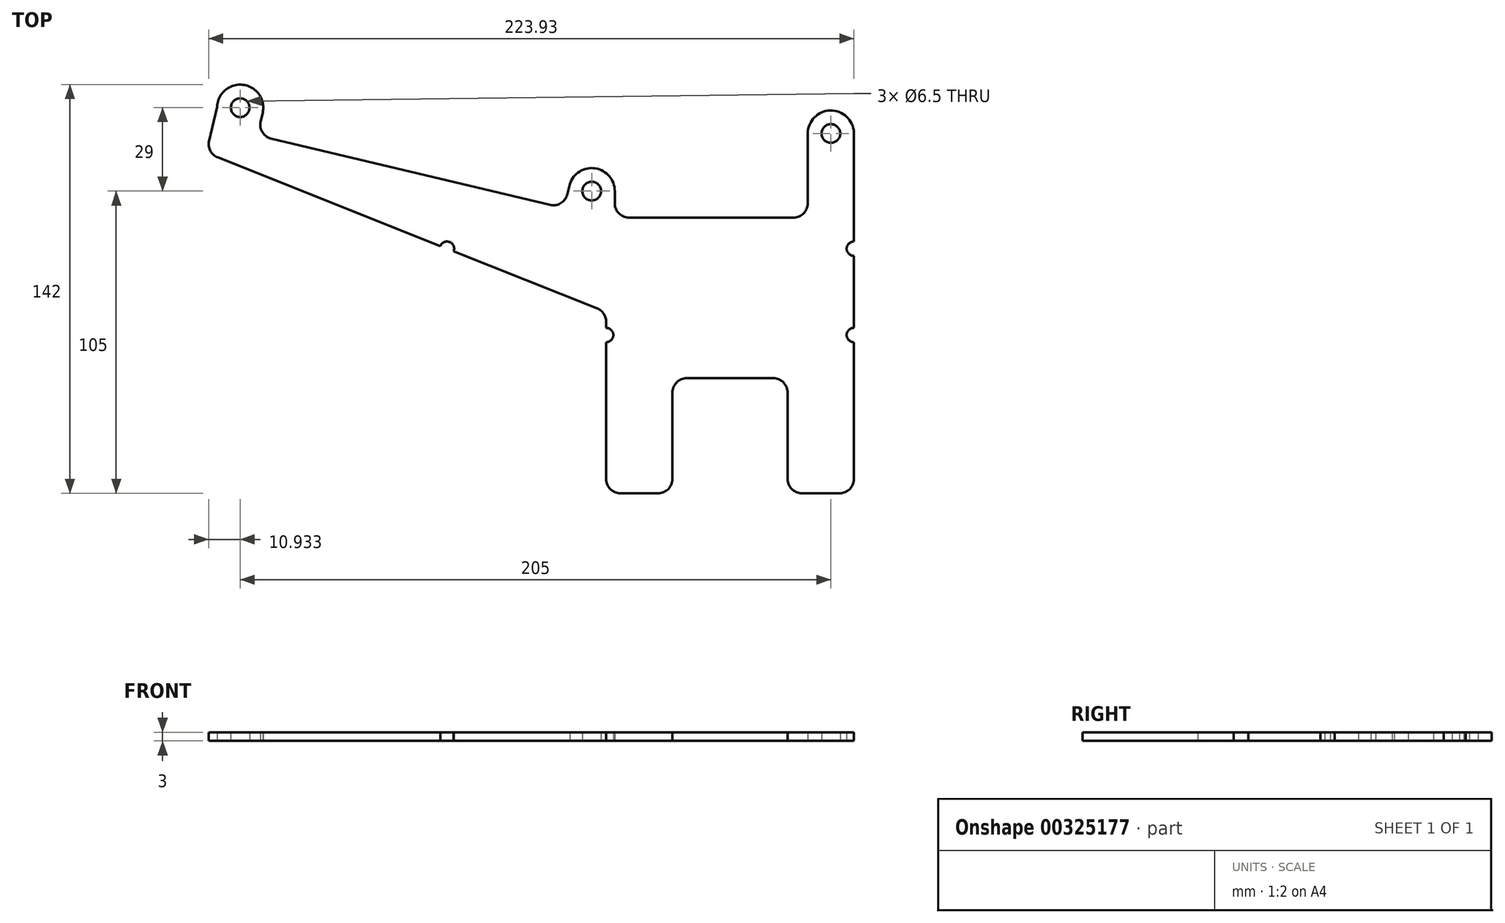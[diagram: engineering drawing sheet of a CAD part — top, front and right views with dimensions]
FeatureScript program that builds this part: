
annotation { "Feature Type Name" : "Feature", "Feature Type Description" : "" }
export const myFeature = defineFeature(function(context is Context, id is Id, definition is map)
    precondition{}
    {
        {
            var Q0;
            Q0=qCreatedBy(makeId("Top.planeOp"),FACE);
            var sketch = newSketch(context, id + "F0", { "sketchPlane" : qUnion([Q0])});
            skCircle(sketch, "E0", {"center": v(216.02, 40) * mm, "radius": 3.25 * mm});
            skCircle(sketch, "E1", {"center": v(133.02, 20) * mm, "radius": 3.25 * mm});
            skCircle(sketch, "E2", {"center": v(11.02, 49) * mm, "radius": 3.25 * mm});
            skLineSegment(sketch, "E3", {"start": v(219.02, -85) * mm, "end": v(206.02, -85) * mm});
            skLineSegment(sketch, "E4", {"start": v(201.02, -80) * mm, "end": v(201.02, -50) * mm});
            skLineSegment(sketch, "E5", {"start": v(196.02, -45) * mm, "end": v(166.02, -45) * mm});
            skLineSegment(sketch, "E6", {"start": v(161.02, -50) * mm, "end": v(161.02, -80) * mm});
            skLineSegment(sketch, "E7", {"start": v(156.02, -85) * mm, "end": v(143.02, -85) * mm});
            skArc(sketch, "E8", {"start": v(224.02, 39.66) * mm, "mid": v(216.2, 48) * mm, "end": v(208.02, 40) * mm});
            skArc(sketch, "E9", {"start": v(141.02, 19.98) * mm, "mid": v(133.66, 27.97) * mm, "end": v(125.12, 21.24) * mm});
            skArc(sketch, "E10", {"start": v(18.75, 46.93) * mm, "mid": v(12.2, 56.91) * mm, "end": v(3.03, 49.27) * mm});
            skLineSegment(sketch, "E11", {"start": v(224.02, 40.34) * mm, "end": v(224.02, 2.5) * mm});
            skLineSegment(sketch, "E12", {"start": v(208.02, 40) * mm, "end": v(208.02, 15.79) * mm});
            skLineSegment(sketch, "E13", {"start": v(203.02, 10.79) * mm, "end": v(146.02, 10.79) * mm});
            skLineSegment(sketch, "E14", {"start": v(141.02, 19.98) * mm, "end": v(141.02, 15.79) * mm});
            skPoint(sketch, "E15.visualSharp", {"position": v(208.02, 10.79) * mm});
            skArc(sketch, "E15.filletArc", {"start": v(203.02, 10.79) * mm, "mid": v(206.56, 12.25) * mm, "end": v(208.02, 15.79) * mm});
            skPoint(sketch, "E16.visualSharp", {"position": v(141.02, 10.79) * mm});
            skArc(sketch, "E16.filletArc", {"start": v(141.02, 15.79) * mm, "mid": v(142.49, 12.25) * mm, "end": v(146.02, 10.79) * mm});
            skPoint(sketch, "E17.visualSharp", {"position": v(224.02, -85) * mm});
            skArc(sketch, "E17.filletArc", {"start": v(219.02, -85) * mm, "mid": v(222.55, -83.54) * mm, "end": v(224.02, -80) * mm});
            skPoint(sketch, "E18.visualSharp", {"position": v(201.02, -85) * mm});
            skArc(sketch, "E18.filletArc", {"start": v(201.02, -80) * mm, "mid": v(202.49, -83.54) * mm, "end": v(206.02, -85) * mm});
            skPoint(sketch, "E19.visualSharp", {"position": v(201.02, -45) * mm});
            skArc(sketch, "E19.filletArc", {"start": v(201.02, -50) * mm, "mid": v(199.56, -46.46) * mm, "end": v(196.02, -45) * mm});
            skPoint(sketch, "E20.visualSharp", {"position": v(161.02, -45) * mm});
            skArc(sketch, "E20.filletArc", {"start": v(166.02, -45) * mm, "mid": v(162.49, -46.46) * mm, "end": v(161.02, -50) * mm});
            skPoint(sketch, "E21.visualSharp", {"position": v(161.02, -85) * mm});
            skArc(sketch, "E21.filletArc", {"start": v(156.02, -85) * mm, "mid": v(159.56, -83.54) * mm, "end": v(161.02, -80) * mm});
            skLineSegment(sketch, "E22", {"start": v(21.82, 38.22) * mm, "end": v(118.55, 15.22) * mm});
            skLineSegment(sketch, "E23", {"start": v(18.86, 47.37) * mm, "end": v(18.11, 44.24) * mm});
            skLineSegment(sketch, "E24", {"start": v(125.4, 22.45) * mm, "end": v(124.57, 18.93) * mm});
            skArc(sketch, "E25.filletArc", {"start": v(118.55, 15.22) * mm, "mid": v(122.33, 15.83) * mm, "end": v(124.57, 18.93) * mm});
            skArc(sketch, "E26.filletArc", {"start": v(18.11, 44.24) * mm, "mid": v(18.72, 40.46) * mm, "end": v(21.82, 38.22) * mm});
            skLineSegment(sketch, "E27", {"start": v(3.03, 49.27) * mm, "end": v(0.22, 37.48) * mm});
            skLineSegment(sketch, "E28", {"start": v(138.02, -80) * mm, "end": v(138.02, -32.5) * mm});
            skLineSegment(sketch, "E29", {"start": v(134.87, -20.75) * mm, "end": v(85.1, -0.92) * mm});
            skPoint(sketch, "E30.visualSharp", {"position": v(-0.78, 33.28) * mm});
            skArc(sketch, "E30.filletArc", {"start": v(0.22, 37.48) * mm, "mid": v(0.65, 34.02) * mm, "end": v(3.24, 31.68) * mm});
            skPoint(sketch, "E31.visualSharp", {"position": v(138.02, -85) * mm});
            skArc(sketch, "E31.filletArc", {"start": v(138.02, -80) * mm, "mid": v(139.49, -83.54) * mm, "end": v(143.02, -85) * mm});
            skPoint(sketch, "E32.visualSharp", {"position": v(138.02, -22) * mm});
            skArc(sketch, "E32.filletArc", {"start": v(138.02, -25.4) * mm, "mid": v(137.16, -22.58) * mm, "end": v(134.87, -20.75) * mm});
            skLineSegment(sketch, "E33", {"start": v(140.52, -30) * mm, "end": v(221.52, -30) * mm});
            skArc(sketch, "E34", {"start": v(224.02, -27.5) * mm, "mid": v(221.52, -30) * mm, "end": v(224.02, -32.5) * mm});
            skArc(sketch, "E35", {"start": v(138.02, -32.5) * mm, "mid": v(140.52, -30) * mm, "end": v(138.02, -27.5) * mm});
            skArc(sketch, "E36", {"start": v(224.02, 2.5) * mm, "mid": v(221.52, 0) * mm, "end": v(224.02, -2.5) * mm});
            skArc(sketch, "E37", {"start": v(85.1, -0.92) * mm, "mid": v(83.7, 2.32) * mm, "end": v(80.46, 0.92) * mm});
            skLineSegment(sketch, "E38.trimOffspring", {"start": v(80.46, 0.92) * mm, "end": v(3.24, 31.68) * mm});
            skLineSegment(sketch, "E39.trimOffspring", {"start": v(138.02, -27.5) * mm, "end": v(138.02, -25.4) * mm});
            skLineSegment(sketch, "E40.trimOffspring", {"start": v(224.02, -32.5) * mm, "end": v(224.02, -80) * mm});
            skLineSegment(sketch, "E41.trimOffspring", {"start": v(224.02, -2.5) * mm, "end": v(224.02, -27.5) * mm});
            skSolve(sketch);
        }
        {
            var Q0;
            Q0=makeQuery(id+"F0.imprint","IMPRINT",FACE,{"disambiguationData":[TD([[makeQuery(id+"F0.imprint","IMPRINT",EDGE,{"derivedFrom":sQuery(id+"F0.wireOp",EDGE,"E0")}),-1.0]])]});
            var Q1;
            Q1=makeQuery(id+"F0.imprint","IMPRINT",FACE,{"disambiguationData":[TD([[makeQuery(id+"F0.imprint","IMPRINT",EDGE,{"derivedFrom":sQuery(id+"F0.wireOp",EDGE,"E3")}),-1.0]])]});
            extrude(context, id + "F1", {"entities" : qUnion([Q0, Q1]), "depth" : 3 * mm});
        }
    });
